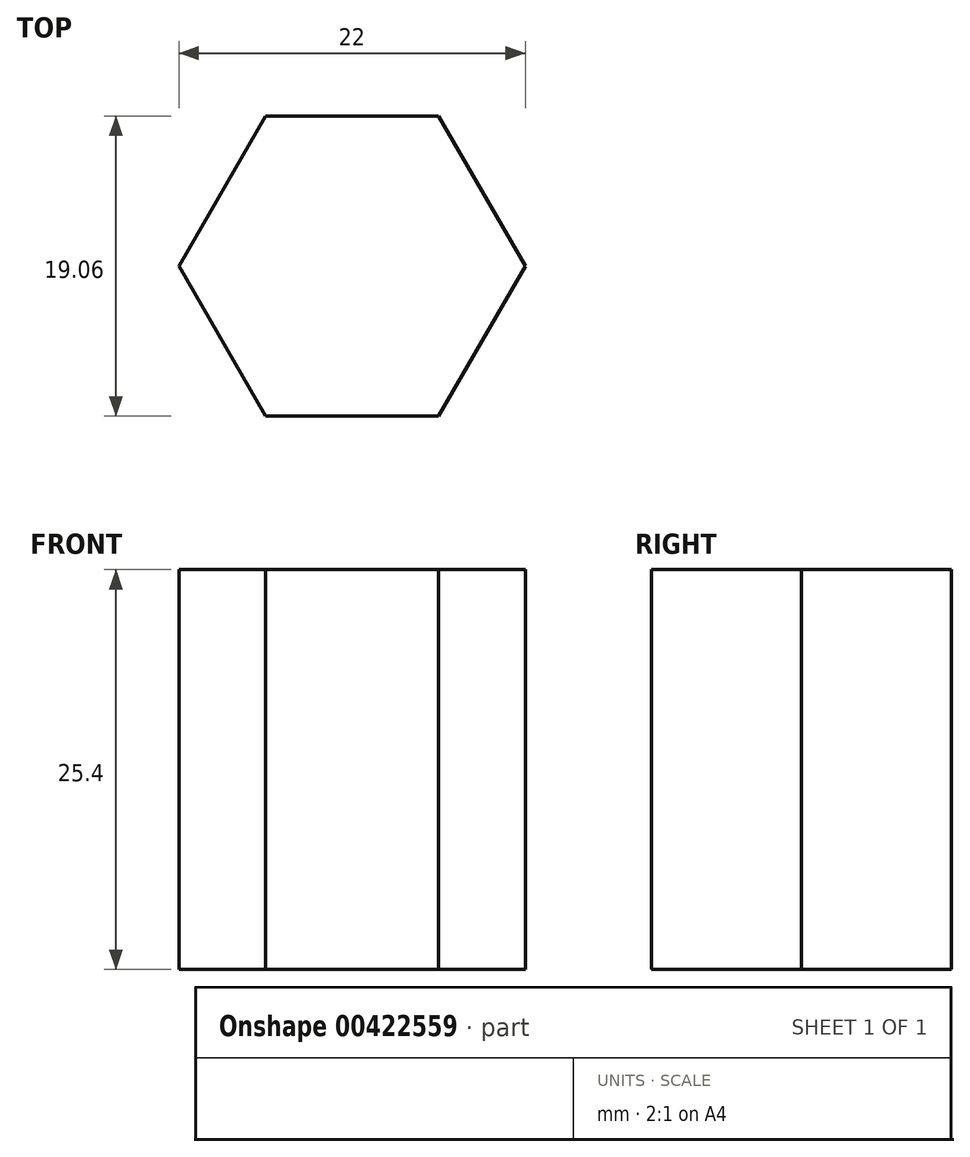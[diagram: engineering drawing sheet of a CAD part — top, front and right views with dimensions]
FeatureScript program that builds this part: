
annotation { "Feature Type Name" : "Feature", "Feature Type Description" : "" }
export const myFeature = defineFeature(function(context is Context, id is Id, definition is map)
    precondition{}
    {
        {
            var Q0;
            Q0=qCreatedBy(makeId("Top.planeOp"),FACE);
            var sketch = newSketch(context, id + "F0", { "sketchPlane" : qUnion([Q0])});
            skCircle(sketch, "E0.cCircle", {"center": v(0, 0) * mm, "radius": 9.53 * mm, "construction": true});
            skLineSegment(sketch, "E0.0", {"start": v(-5.5, 9.53) * mm, "end": v(5.5, 9.53) * mm});
            skLineSegment(sketch, "E0.1", {"start": v(5.5, 9.52) * mm, "end": v(11, 0) * mm});
            skLineSegment(sketch, "E0.2", {"start": v(11, 0) * mm, "end": v(5.5, -9.53) * mm});
            skLineSegment(sketch, "E0.3", {"start": v(5.5, -9.52) * mm, "end": v(-5.5, -9.53) * mm});
            skLineSegment(sketch, "E0.4", {"start": v(-5.5, -9.53) * mm, "end": v(-11, 0) * mm});
            skLineSegment(sketch, "E0.5", {"start": v(-11, 0) * mm, "end": v(-5.5, 9.52) * mm});
            skPoint(sketch, "E0.0.midPoint", {"position": v(0, 9.53) * mm});
            skSolve(sketch);
        }
        {
            var Q0;
            Q0 = qSketchRegion(id + "F0", true);
            extrude(context, id + "F1", {"entities" : qUnion([Q0]), "depth" : 25.4 * mm});
        }
    });
